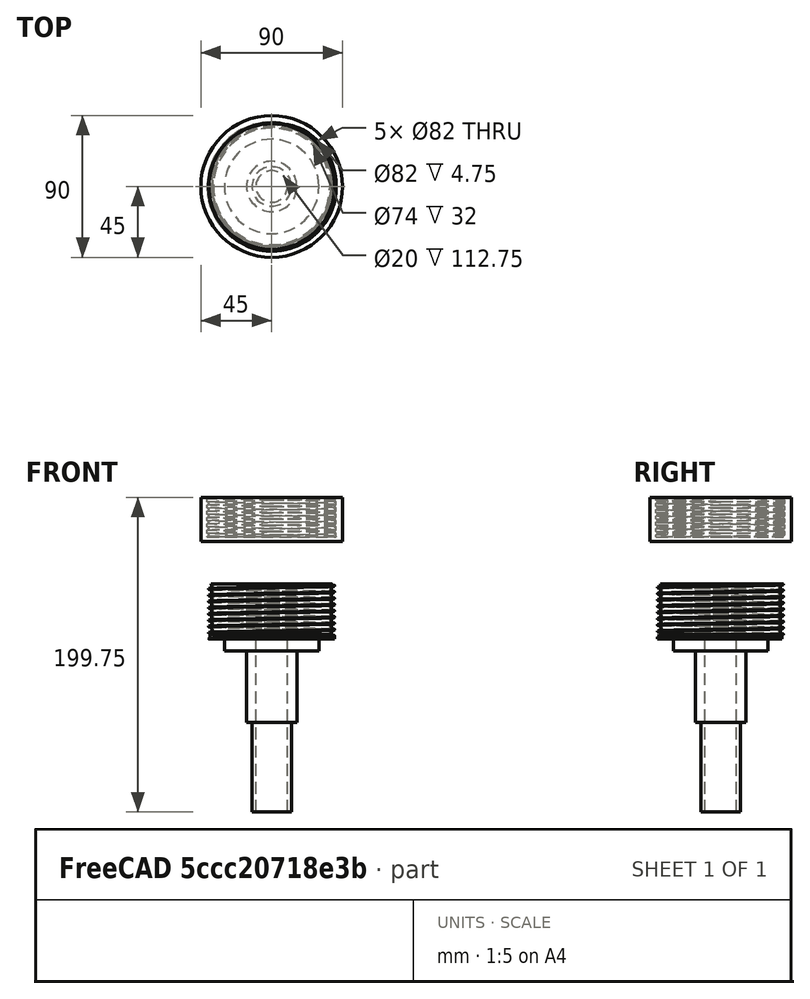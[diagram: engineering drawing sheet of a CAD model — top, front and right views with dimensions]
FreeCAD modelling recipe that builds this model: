
FCSTD DOCUMENT  (FreeCAD 0.18R16131 (Git))
Label: caixa slave
License: All rights reserved
LicenseURL: http://en.wikipedia.org/wiki/All_rights_reserved
objects: Part::Cylinder×10, Part::Cut×7, Part::MultiFuse×7, Part::FeaturePython×5, Part::Circle×3, Part::Sweep×3, Part::Box×3, Part::Helix×2, Part::Plane×2, App::DocumentObjectGroup×2
note: 42 computed .brp shape members not serialized (recipe doc carries the construction recipe); baked Part::Feature solids carry a one-line shape summary decoded from their .brp

FEATURE [Part::Cylinder] Cylinder
  Angle = 360
  AttacherType = Attacher::AttachEngine3D
  Height = 35
  Radius = 45
FEATURE [Part::Cylinder] Cylinder001
  Angle = 360
  AttacherType = Attacher::AttachEngine3D
  Height = 35
  Radius = 41
FEATURE [Part::Cut] Cut
  Base = -> Cylinder
  Refine = true
  Tool = -> Cylinder001
FEATURE [Part::Helix] Helix
  Angle = 0
  AttacherType = Attacher::AttachEngine3D
  Height = 40
  LocalCoord = 0
  Pitch = 4
  Radius = 41
  Style = 1
FEATURE [Part::Cylinder] Cylinder002
  Angle = 360
  AttacherType = Attacher::AttachEngine3D
  Height = 35
  Radius = 40
FEATURE [Part::Circle] Circle
  Angle0 = 0
  Angle1 = 360
  AttacherType = Attacher::AttachEngine3D
  Placement = pos=(-41,0,2) rot=(1,0,0;1.5708rad)
  Radius = 1
FEATURE [Part::Sweep] Sweep  label="pequeno"
  Frenet = false
  Sections = -> [Circle]
  Solid = true
  Spine = -> Helix [Edge1,Edge2,Edge3,Edge4,Edge5,Edge6,Edge7,Edge8,Edge9,Edge10]
  Transition = 1
FEATURE [Part::Circle] Circle001
  Angle0 = 0
  Angle1 = 360
  AttacherType = Attacher::AttachEngine3D
  Placement = pos=(-41.75,0,1.25) rot=(1,0,0;1.5708rad)
  Radius = 1.5
FEATURE [Part::Sweep] Sweep001  label="grande"
  Frenet = false
  Sections = -> [Circle001]
  Solid = false
  Spine = -> Helix [Edge1,Edge2,Edge3,Edge4,Edge5,Edge6,Edge7,Edge8,Edge9,Edge10]
  Transition = 1
FEATURE [Part::MultiFuse] Fusion
  Refine = true
  Shapes = -> [Cut,Sweep]
FEATURE [Part::Box] Box  label="Cube"
  AttacherType = Attacher::AttachEngine3D
  Height = 10
  Length = 100
  Placement = pos=(-55.75,-50.25,35.25) rot=(0,0,1;0rad)
  Width = 100
FEATURE [Part::Cut] Cut001
  Base = -> Fusion
  Refine = true
  Tool = -> Box
FEATURE [Part::Cylinder] Cylinder003
  Angle = 360
  AttacherType = Attacher::AttachEngine3D
  Height = 3
  Placement = pos=(0,0,-2.25) rot=(0,0,1;0rad)
  Radius = 45
FEATURE [Part::MultiFuse] Fusion001
  Placement = pos=(0,0,64.25) rot=(0,0,1;0rad)
  Refine = true
  Shapes = -> [Cylinder003,Cut001]
FEATURE [Part::Helix] Helix001
  Angle = 0
  AttacherType = Attacher::AttachEngine3D
  Height = 40
  LocalCoord = 0
  Pitch = 4
  Radius = 40
  Style = 1
FEATURE [Part::Circle] Circle002
  Angle0 = 0
  Angle1 = 360
  AttacherType = Attacher::AttachEngine3D
  Placement = pos=(39.75,0,0) rot=(-1,0,0;1.5708rad)
  Radius = 1.75
FEATURE [Part::Sweep] Sweep002
  Frenet = false
  Sections = -> [Circle002]
  Solid = true
  Spine = -> Helix001 [Edge1,Edge2,Edge3,Edge4,Edge5,Edge6,Edge7,Edge8,Edge9,Edge10]
  Transition = 1
FEATURE [Part::Cut] Cut002
  Base = -> Cylinder002
  Refine = true
  Tool = -> Sweep002
FEATURE [Part::Box] Box001  label="Cube001"
  AttacherType = Attacher::AttachEngine3D
  Height = 10
  Length = 100
  Placement = pos=(-51.25,-45.75,-9.5) rot=(0,0,1;0rad)
  Width = 100
FEATURE [Part::Cut] Cut003
  Base = -> Cut002
  Refine = true
  Tool = -> Box001
FEATURE [Part::Cylinder] Cylinder004
  Angle = 360
  AttacherType = Attacher::AttachEngine3D
  Height = 50
  Radius = 37
FEATURE [Part::Cut] Cut004
  Base = -> Cut003
  Refine = true
  Tool = -> Cylinder004
FEATURE [Part::Cylinder] Cylinder005
  Angle = 360
  AttacherType = Attacher::AttachEngine3D
  Height = 3
  Radius = 39
FEATURE [Part::MultiFuse] Fusion002
  Refine = true
  Shapes = -> [Cut004,Cylinder005]
FEATURE [Part::Cylinder] Cylinder006
  Angle = 360
  AttacherType = Attacher::AttachEngine3D
  Height = 100
  Radius = 16
FEATURE [Part::Cylinder] Cylinder008
  Angle = 360
  AttacherType = Attacher::AttachEngine3D
  Height = 60
  Placement = pos=(0,0,99.75) rot=(0,0,1;0rad)
  Radius = 12.5
FEATURE [Part::Cylinder] Cylinder009
  Angle = 360
  AttacherType = Attacher::AttachEngine3D
  Height = 250
  Placement = pos=(0,0,-168.75) rot=(0,0,1;0rad)
  Radius = 10
FEATURE [Part::MultiFuse] Fusion003
  Placement = pos=(1e-15,0,-7) rot=(0,1,0;3.14159rad)
  Refine = true
  Shapes = -> [Cylinder008,Cylinder006]
FEATURE [Part::Cylinder] Cylinder010
  Angle = 360
  AttacherType = Attacher::AttachEngine3D
  Height = 8
  Placement = pos=(0,0,-7.5) rot=(0,0,1;0rad)
  Radius = 30
FEATURE [Part::MultiFuse] Fusion004
  Refine = true
  Shapes = -> [Fusion003,Cylinder010]
FEATURE [Part::MultiFuse] Fusion005
  Refine = true
  Shapes = -> [Fusion002,Fusion004]
FEATURE [Part::Cut] Cut005
  Base = -> Fusion005
  Refine = true
  Tool = -> Cylinder009
FEATURE [Part::Box] Box002  label="Cube002"
  AttacherType = Attacher::AttachEngine3D
  Height = 10
  Length = 100
  Placement = pos=(-47,-48,90) rot=(0,0,1;0rad)
  Width = 100
FEATURE [Part::Cut] Cut006
  Base = -> Fusion001
  Refine = true
  Tool = -> Box002
FEATURE [Part::Plane] Plane
  AttacherType = Attacher::AttachEngine3D
  Length = 100
  Placement = pos=(-49,-39,-53) rot=(0,0,1;0rad)
  Width = 100
FEATURE [Part::FeaturePython] Slice  # WARN: FeaturePython — macro-defined, semantics opaque (R4)
  Base = -> Cut005
  Mode = 1
  Tolerance = 0
  Tools = -> [Plane]
FEATURE [Part::FeaturePython] Slice_child0  label="Slice.0"  # WARN: FeaturePython — macro-defined, semantics opaque (R4)
  Base = -> Slice
  FilterType = 1
  Invert = false
  OverrideMaxVal = 0
  WindowFrom = 80
  WindowTo = 100
  items = 0
FEATURE [Part::FeaturePython] Slice_child1  label="Slice.1"  # WARN: FeaturePython — macro-defined, semantics opaque (R4)
  Base = -> Slice
  FilterType = 1
  Invert = false
  OverrideMaxVal = 0
  WindowFrom = 80
  WindowTo = 100
  items = 1
FEATURE [Part::Plane] Plane001
  AttacherType = Attacher::AttachEngine3D
  Length = 100
  Placement = pos=(-39,-37,-108) rot=(0,0,1;0rad)
  Width = 100
FEATURE [Part::FeaturePython] Slice001  # WARN: FeaturePython — macro-defined, semantics opaque (R4)
  Base = -> Slice_child1
  Mode = 1
  Tolerance = 0
  Tools = -> [Plane001]
FEATURE [App::DocumentObjectGroup] GrExplode_Slice001  label="Exploded Slice001"
FEATURE [Part::FeaturePython] Slice001_child1  label="Slice001.1"  # WARN: FeaturePython — macro-defined, semantics opaque (R4)
  Base = -> Slice001
  FilterType = 1
  Invert = false
  OverrideMaxVal = 0
  Placement = pos=(0,0,57) rot=(0,0,1;0rad)
  WindowFrom = 80
  WindowTo = 100
  items = 1
FEATURE [Part::MultiFuse] Fusion006
  Refine = true
  Shapes = -> [Slice001_child1,Slice_child0]
FEATURE [App::DocumentObjectGroup] GrExplode_Slice  label="Exploded Slice"
  Group = -> [Slice_child1,Fusion006]
